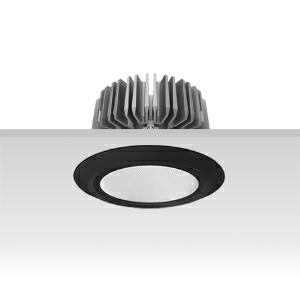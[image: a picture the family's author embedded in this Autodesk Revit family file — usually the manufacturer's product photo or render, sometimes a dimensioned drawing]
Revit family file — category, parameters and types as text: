
# Revit family: 3f_filippi_-_3f_reno_bianco_ampio_3f_filippi_-_30379_a01036_-_3f_reno_150_wh_2000-930_dali_wide___vs_bk_699a
name_source: partatom
category: Lighting Fixtures
units: mm (PartAtom-declared; Revit-internal decimal feet)

## family parameters
Cut with Voids When Loaded = No
Host = Face
Light Source = No
Part Type = Normal
Room Calculation Point = No
Round Connector Dimension = Use Diameter
Shared = No

## types (1)
- 3F Filippi - 3F Reno Bianco Ampio (1 x LED, 1636 lm, 24 W, 3000 K)
    Apparent Load = 24 VA
    Approval mark = CE
    CIE Flux Codes = 74 93 99 100 100
    Color Rendering = 90
    Color Temperature = 3000 K
    Control Gear = Electronic transformer
    Default Elevation = 1800 mm
    Description = ILLUMINOTECHNICAL
Luminous efficiency 100% (DLOR 100%, ULOR 0%).
Initial luminous flux of the luminaire 1636 lm.
Direct symmetric wide distribution.
Installation Interdistance Transv.D = 1.12 x hu - Long.D = 1.11 x hu.
Tabular UGR (CIE 117 - 4H-8H; S=0.25H; 70/50/20): RUG 22.7 - 22.5.
Beam angle: 74° - 73°.
Luminous efficacy 68 lm/W.
Lifetime (L90/B10): 30000 h. (tq+25°C)
Lifetime (L85/B10): 50000 h. (tq+25°C)
Lifetime (L70/B10): 80000 h. (tq+25°C)
Sudden decreased luminous flux after 50000 hours: 0% (C0).
Photobiological safety in compliance with IEC/TR 62778: RG0 risk exempt, (IEC 62471).
In compliance with IEC/EN 62722-2-1 - IEC/EN 62717 standards.

SOURCE
Compact LED module 2000/930.
Energy efficiency class (UE 2019/2020 - UE 2019/2015): E.
CIE 13.3 Colour rendering index: CRI >90 (R9 >50%).
IES TM-30 Fidelity Index: Rf = 92 Rg = 101.
CCT nominal colour temperature 3000 K.
Colour initial tolerance (MacAdam): SDCM 3.
Zhaga Book 3 compliant.

MECHANICAL
Passive heat dissipator in die-casting aluminium, oversized, for optimum thermal management of the LED module.
Parabolic element with graduated/concentric rings in white polycarbonate.
Transparent external lens with glossy and satin differentiated surfaces, with a cooling and anti-insect system in methacrylate (PMMA).
Fastening spring clips in stainless steel.
Dimensions: diameter 176 mm, height 111 mm. Weight 0.85 kg.
IP44 protection degree for exposed part, IP20 for recessed part.
Mechanical strength to impacts IK06 (1 joule).
Glow-wire test resistance 650°C.

ELECTRICAL
Wiring on a separate unit.
Halogen Free DALI-2 DATI (Parts 251, 252, 253), PUSH-DIM, electronic wiring 230V-50/60Hz, power factor 0.95 at full load, THD <25%, constant output current, SELV, class II, 1 driver, 1 DALI addresse.
Power of the luminaire 24 W.
ENEC - CE.
SAFE FLICKER: PstLM=<1 and SVM=<0.4 (IEC TR 61547-1 and IEC TR 63158), to ensure a more comfortable and safe light.
Luminaire compliant with EN 60598-2-22 for power supply from a centralised emergency system CPSS (Central Power Supply System), not incorporated in the luminaire - high risk areas excluded. The default power and flux are 100% in AC and 100% in DC.
Ambient temperature from 0°C to +25°C.
Temperature class T6 max 85°C.
Relative humidity UR: <85%.

INSTALLATION
Pull-up recessed fitting.
False ceiling carving: 150 mm.
All accessories dedicated to this product are available on the Catalog and on our website www.3F-Filippi.com.

ACCESSORIES
A01036 - Anti-glare microprismatic VS moulded glass, tempered, not flammable, locked and in line with the trim, in black polycarbonate.

APPLICATIONS
Environments: architectural, commercial, exhibition areas, transit areas, corridors, shops, display windows, service areas.
In false ceilings with narrow voids.

LIGHT MANAGEMENT
Recommended minimum setting: 10%.
The luminaire, equipped with (DALI-2 DATI) driver, can be controlled manually with 3F Easy Dim technology or automatically/manually with wired or wireless DALI/D2D control systems.
The D2D driver guarantees interoperability with other devices with the same certification by making the following information available:
Device Data (Part 251), Energy Report (Part 252), Diagnosis & Maintenance (Part 253).
In electrical systems without a regulation system (manual or automatic) and DALI bus, a suitable jumper must be made on the DA-DA terminals of the appliance.

WARNING
Luminaire designed for disposal/recycling at end-of-life.
Replaceable (LED only) light source by a professional. Replaceable control gear by a professional.
    Height = 0 mm  [stored 0 ft]
    Lamp = 1 x LED
    Lamp Light Flux = 1636 lm
    Lamp Power = 24 W
    Lamp count = 1
    Length = 176 mm
    Lifetime = 50000 h
    Luminous efficacy = 68 lm/W
    Manufacturer = 3F Filippi
    ModVariant = No
    Model = 3F Filippi - 30379+A01036 - 3F Reno 150 WH 2000-930 DALI WIDE + VS BK
    Mounting Place = Ceiling
    Mounting Type = Recessed
    Number of Poles = 1
    OnlyDefault = Yes
    Power Factor = 1
    Product Name = 3F Filippi - 3F Reno Bianco Ampio
    Product group = recessed luminaire
    ProductGroupID = 4
    Protection Class = Protection class II
    Protection Degree = IP 20
    RLX_Detail_Level = 1
    RLX_Emergency_Light_Flux = 0 lm
    RLX_Emergency_Type = 0
    RLX_Emergency_Type_DB = No
    RlxData = <blob elided: 87985 chars, md5=48878e20>
    Socket = socket
    Standby Power = 0 W
    System Light Flux = 1636 lm
    System Power = 24 W
    Type Comments = Product without accessories
    Type Image = 3ffilippi_3f_reno_150_bk_vs_smp.jpg
    URL = http://relux.com
    VarID = ---
    Voltage = 0 V
    Weight = 0.00 kg
    Width = 0 mm  [stored 0 ft]

note: [stored X ft] marks values corroborated as IEEE doubles in the binary element streams (Revit-internal decimal feet)

## geometry (parser evidence)
native form markers: Blend x4, Sweep x12
no freeform markers — native parametric forms only
